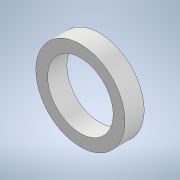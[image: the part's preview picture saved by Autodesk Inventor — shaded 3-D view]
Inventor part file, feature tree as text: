
AUTODESK INVENTOR PART (.ipt)
format: ipt  version: 2022.3 (Build 263350000, 350)  size: 185,856 bytes
history: native  units: mm
features: reference x140, extrude x5, sketch x5, other x5, projected_geometry x2
ambient origin geometry x8: Origin, YZ Plane, XZ Plane, XY Plane, X Axis, Y Axis, Z Axis, Center Point
bodies: Solid1 (feature_tree)
feature tree (157):
  extrude  "Extrusion1"  Depth=2.5mm TaperAngle=0.0deg
  extrude  "Extrusion2"  Depth=2.0mm TaperAngle=0.0deg
  extrude  "Extrusion3"  Depth=10.0mm TaperAngle=0.0deg
  extrude  "Extrusion4"  [1 undecoded]
  extrude  "Extrusion5"  [1 undecoded]
  sketch  "Sketch1"  dims[d0=1.0mm d1=2.5mm d2=0.0mm]
  reference  "Reference1"
  reference  "Reference2"
  reference  "Reference3"
  reference  "Reference4"
  reference  "Reference5"
  reference  "Reference6"
  reference  "Reference7"
  reference  "Reference8"
  reference  "Reference9"
  reference  "Reference10"
  reference  "Reference11"
  reference  "Reference12"
  reference  "Reference13"
  reference  "Reference14"
  reference  "Reference15"
  reference  "Reference16"
  reference  "Reference17"
  reference  "Reference18"
  reference  "Reference19"
  reference  "Reference20"
  reference  "Reference21"
  reference  "Reference22"
  reference  "Reference23"
  reference  "Reference24"
  reference  "Reference25"
  reference  "Reference26"
  reference  "Reference27"
  reference  "Reference28"
  reference  "Reference29"
  reference  "Reference30"
  reference  "Reference31"
  reference  "Reference32"
  reference  "Reference33"
  reference  "Reference34"
  reference  "Reference35"
  reference  "Reference36"
  reference  "Reference37"
  reference  "Reference38"
  reference  "Reference39"
  reference  "Reference40"
  reference  "Reference41"
  reference  "Reference42"
  reference  "Reference43"
  reference  "Reference44"
  reference  "Reference45"
  reference  "Reference46"
  reference  "Reference47"
  reference  "Reference48"
  reference  "Reference49"
  reference  "Reference50"
  reference  "Reference51"
  reference  "Reference52"
  reference  "Reference53"
  reference  "Reference54"
  reference  "Reference55"
  reference  "Reference56"
  reference  "Reference57"
  reference  "Reference58"
  reference  "Reference59"
  reference  "Reference60"
  reference  "Reference61"
  reference  "Reference62"
  reference  "Reference63"
  reference  "Reference64"
  reference  "Reference65"
  reference  "Reference66"
  reference  "Reference67"
  reference  "Reference68"
  reference  "Reference69"
  reference  "Reference70"
  reference  "Reference71"
  reference  "Reference72"
  reference  "Reference73"
  reference  "Reference74"
  reference  "Reference75"
  reference  "Reference76"
  reference  "Reference77"
  reference  "Reference78"
  reference  "Reference79"
  reference  "Reference80"
  reference  "Reference81"
  reference  "Reference82"
  reference  "Reference83"
  reference  "Reference84"
  reference  "Reference85"
  reference  "Reference86"
  reference  "Reference87"
  reference  "Reference88"
  reference  "Reference89"
  reference  "Reference90"
  reference  "Reference91"
  reference  "Reference92"
  reference  "Reference93"
  reference  "Reference94"
  reference  "Reference95"
  reference  "Reference96"
  reference  "Reference97"
  reference  "Reference98"
  reference  "Reference99"
  reference  "Reference100"
  reference  "Reference101"
  reference  "Reference102"
  reference  "Reference103"
  reference  "Reference104"
  reference  "Reference105"
  reference  "Reference106"
  reference  "Reference107"
  reference  "Reference108"
  reference  "Reference109"
  reference  "Reference110"
  reference  "Reference111"
  reference  "Reference112"
  reference  "Reference113"
  reference  "Reference114"
  reference  "Reference115"
  reference  "Reference116"
  reference  "Reference117"
  reference  "Reference118"
  reference  "Reference119"
  reference  "Reference120"
  reference  "Reference121"
  reference  "Reference122"
  reference  "Reference123"
  reference  "Reference124"
  reference  "Reference125"
  reference  "Reference126"
  reference  "Reference127"
  reference  "Reference128"
  reference  "Reference129"
  reference  "Reference130"
  reference  "Reference131"
  reference  "Reference132"
  reference  "Reference133"
  reference  "Reference134"
  reference  "Reference135"
  reference  "Reference136"
  reference  "Reference137"
  reference  "Reference138"
  sketch  "Sketch2"  dims[d3=2.0mm d4=0.0mm d5=2.0mm d6=0.0mm]
  projected_geometry  "Projected Loop1"
  reference  "Reference139"
  sketch  "Sketch3"  dims[d7=0.4mm d8=0.0mm d9=10.0mm d10=0.0mm]
  reference  "Reference140"
  sketch  "Sketch4"
  projected_geometry  "Projected Loop2"
  sketch  "Sketch5"
  other  "Assembly1"
  other  "Moteur - Engrenage 3:2"
  other  "Moteur - Engrenage 4:1"
  other  "Moteur - Engrenage 4:2"
  other  "Moteur - Engrenage 3:1"
note: 2 required parameter values undecoded (feature->parameter linkage not recoverable at this tier; creation-order binding heuristic only, values carry confidence <= 0.55)
